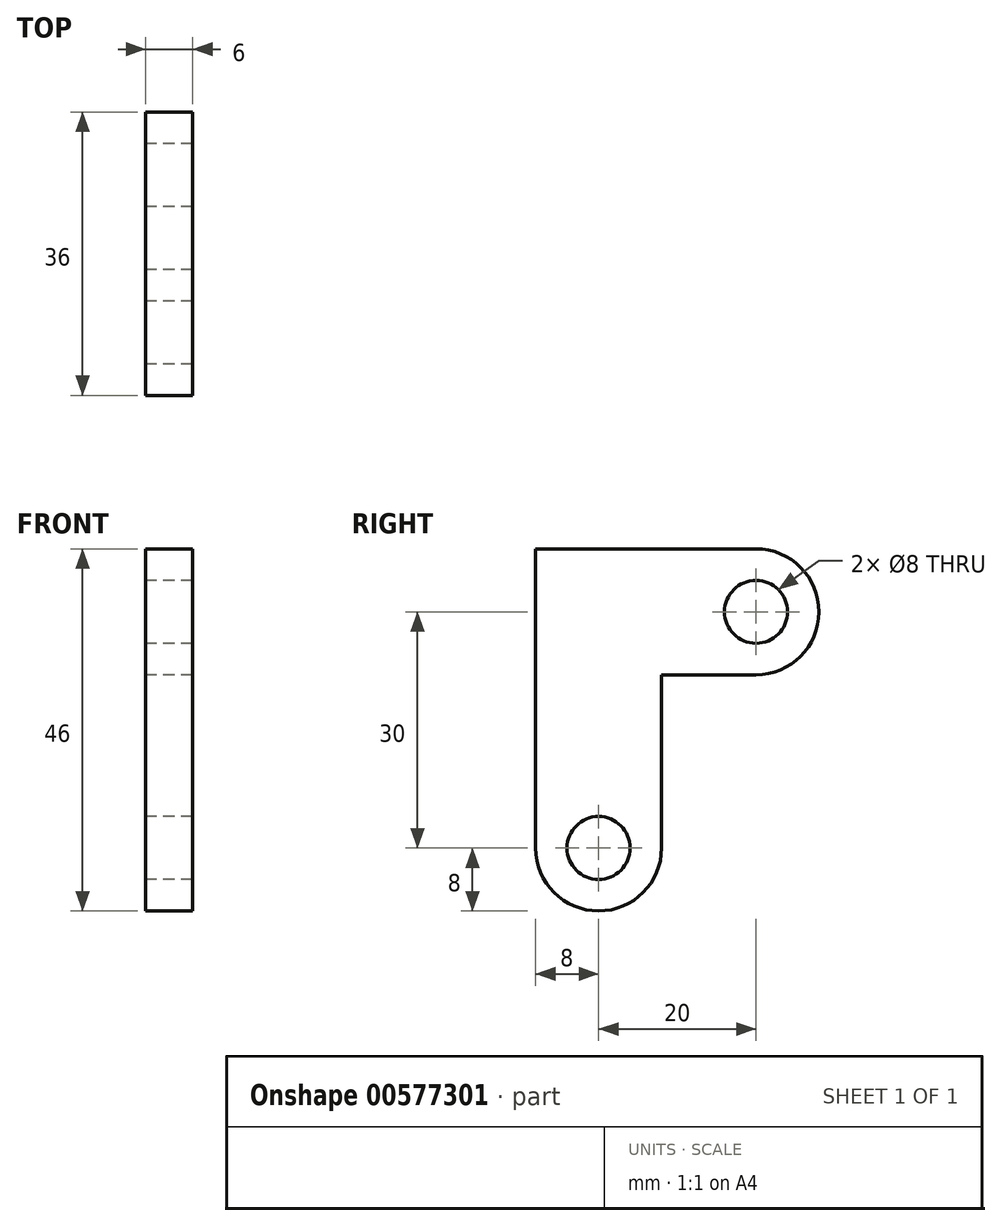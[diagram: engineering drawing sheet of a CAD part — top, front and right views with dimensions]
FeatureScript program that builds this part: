
annotation { "Feature Type Name" : "Feature", "Feature Type Description" : "" }
export const myFeature = defineFeature(function(context is Context, id is Id, definition is map)
    precondition{}
    {
        {
            var Q0;
            Q0=qCreatedBy(makeId("Right.planeOp"),FACE);
            var sketch = newSketch(context, id + "F0", { "sketchPlane" : qUnion([Q0])});
            skCircle(sketch, "E0", {"center": v(0, 0) * mm, "radius": 4 * mm});
            skCircle(sketch, "E1", {"center": v(-20, -30) * mm, "radius": 4 * mm});
            skArc(sketch, "E2", {"start": v(0, -8) * mm, "mid": v(8, 0) * mm, "end": v(0, 8) * mm});
            skArc(sketch, "E3", {"start": v(-28, -30) * mm, "mid": v(-20, -38) * mm, "end": v(-12, -30) * mm});
            skLineSegment(sketch, "E4", {"start": v(-28, -30) * mm, "end": v(-28, 8) * mm});
            skLineSegment(sketch, "E5", {"start": v(0, 8) * mm, "end": v(-28, 8) * mm});
            skLineSegment(sketch, "E6", {"start": v(-12, -30) * mm, "end": v(-12, -8) * mm});
            skLineSegment(sketch, "E7", {"start": v(0, -8) * mm, "end": v(-12, -8) * mm});
            skSolve(sketch);
        }
        {
            var Q0;
            Q0 = qSketchRegion(id + "F0", true);
            extrude(context, id + "F1", {"entities" : qUnion([Q0]), "depth" : 6 * mm, "offsetDistance" : 25 * mm});
        }
    });
